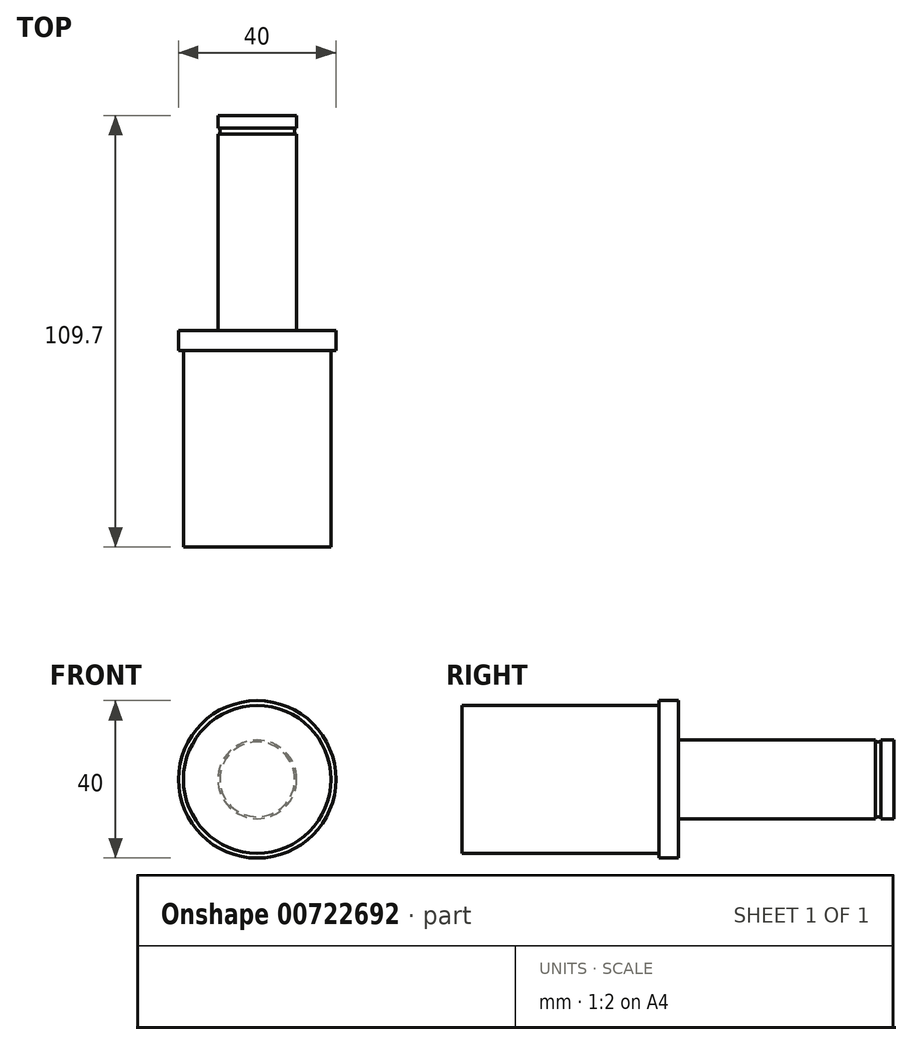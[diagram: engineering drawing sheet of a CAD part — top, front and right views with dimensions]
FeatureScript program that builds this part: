
annotation { "Feature Type Name" : "Feature", "Feature Type Description" : "" }
export const myFeature = defineFeature(function(context is Context, id is Id, definition is map)
    precondition{}
    {
        {
            var Q0;
            Q0=qCreatedBy(makeId("Front.planeOp"),FACE);
            var sketch = newSketch(context, id + "F0", { "sketchPlane" : qUnion([Q0])});
            skCircle(sketch, "E0", {"center": v(0, 0) * mm, "radius": 18.75 * mm});
            skSolve(sketch);
        }
        {
            var Q0;
            Q0 = qSketchRegion(id + "F0", true);
            extrude(context, id + "F1", {"entities" : qUnion([Q0]), "depth" : 50 * mm, "offsetDistance" : 25 * mm});
        }
        {
            var Q0;
            Q0=qCreatedBy(makeId("Front.planeOp"),FACE);
            var sketch = newSketch(context, id + "F2", { "sketchPlane" : qUnion([Q0])});
            skCircle(sketch, "E1", {"center": v(0, 0) * mm, "radius": 20 * mm});
            skSolve(sketch);
        }
        {
            var Q0;
            Q0 = qSketchRegion(id + "F2", true);
            extrude(context, id + "F3", {"entities" : qUnion([Q0]), "operationType" : NewBodyOperationType.ADD, "oppositeDirection" : true, "depth" : 5 * mm, "offsetDistance" : 25 * mm});
        }
        {
            var Q0;
            Q0=makeQuery(id+"F3.opExtrude","CAP_FACE",FACE,{"disambiguationData":[OSD([sQuery(id+"F2.wireOp",EDGE,"E1")])],"isStart":false});
            cPlane(context, id + "F4", {"entities" : qUnion([Q0]), "cplaneType" : CPlaneType.OFFSET, "offset" : 0 * mm, "width" : 150 * mm, "height" : 150 * mm});
        }
        {
            var Q0;
            Q0=qCreatedBy(id+"F4.planeOp",FACE);
            var sketch = newSketch(context, id + "F5", { "sketchPlane" : qUnion([Q0])});
            skCircle(sketch, "E2", {"center": v(0, 0) * mm, "radius": 10 * mm});
            skSolve(sketch);
        }
        {
            var Q0;
            Q0 = qSketchRegion(id + "F5", true);
            extrude(context, id + "F6", {"entities" : qUnion([Q0]), "operationType" : NewBodyOperationType.ADD, "depth" : 50 * mm, "offsetDistance" : 25 * mm});
        }
        {
            var Q0;
            Q0=makeQuery(id+"F6.opExtrude","CAP_FACE",FACE,{"disambiguationData":[OSD([sQuery(id+"F5.wireOp",EDGE,"E2")])],"isStart":false});
            cPlane(context, id + "F7", {"entities" : qUnion([Q0]), "cplaneType" : CPlaneType.OFFSET, "offset" : 0 * mm, "width" : 150 * mm, "height" : 150 * mm});
        }
        {
            var Q0;
            Q0=qCreatedBy(id+"F7.planeOp",FACE);
            var sketch = newSketch(context, id + "F8", { "sketchPlane" : qUnion([Q0])});
            skCircle(sketch, "E3", {"center": v(0, 0) * mm, "radius": 9.5 * mm});
            skSolve(sketch);
        }
        {
            var Q0;
            Q0 = qSketchRegion(id + "F8", true);
            extrude(context, id + "F9", {"entities" : qUnion([Q0]), "operationType" : NewBodyOperationType.ADD, "depth" : 1.5 * mm, "offsetDistance" : 25 * mm});
        }
        {
            var Q0;
            Q0=makeQuery(id+"F9.opExtrude","CAP_FACE",FACE,{"disambiguationData":[OSD([sQuery(id+"F8.wireOp",EDGE,"E3")])],"isStart":false});
            cPlane(context, id + "F10", {"entities" : qUnion([Q0]), "cplaneType" : CPlaneType.OFFSET, "offset" : 0 * mm, "width" : 150 * mm, "height" : 150 * mm});
        }
        {
            var Q0;
            Q0=qCreatedBy(id+"F10.planeOp",FACE);
            var sketch = newSketch(context, id + "F11", { "sketchPlane" : qUnion([Q0])});
            skCircle(sketch, "E4", {"center": v(0, 0) * mm, "radius": 10 * mm});
            skSolve(sketch);
        }
        {
            var Q0;
            Q0 = qSketchRegion(id + "F11", true);
            extrude(context, id + "F12", {"entities" : qUnion([Q0]), "operationType" : NewBodyOperationType.ADD, "depth" : 3.2 * mm, "offsetDistance" : 25 * mm});
        }
    });
